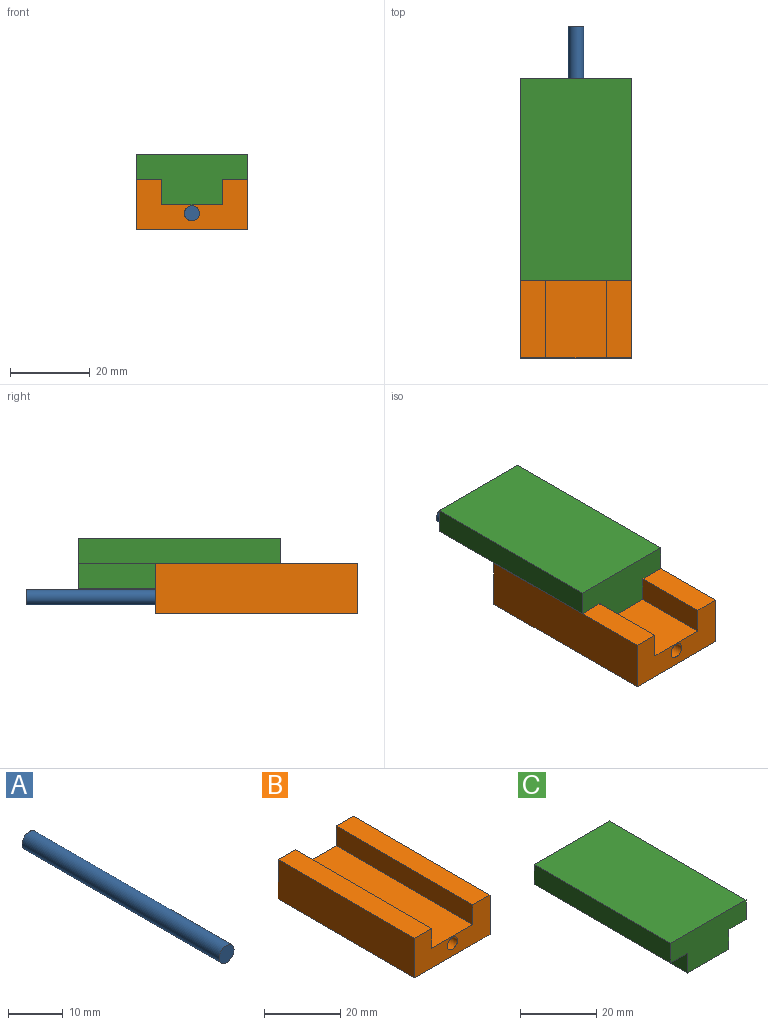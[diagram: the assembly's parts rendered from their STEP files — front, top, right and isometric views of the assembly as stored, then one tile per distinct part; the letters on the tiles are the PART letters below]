
ASSEMBLY  parts=3 mates=3
PART A: 3 faces, bbox 3.8x50.8x3.8 mm
  f0: cylinder r=1.91mm len=50.8mm, axis (0,1,0), area 608mm2, adj f1,f2
  f1: plane 3.81x3.81mm, normal (0,-1,0), area 11.4mm2, adj f0
  f2: plane 3.81x3.81mm, normal (0,1,0), area 11.4mm2, adj f0
PART B: 11 faces, bbox 27.9x50.8x12.7 mm
  f0: plane 50.8x12.7mm, normal (-1,0,0), area 645.2mm2, adj f1,f7,f8,f9
  f1: plane 50.8x27.94mm, normal (0,0,-1), area 1419.4mm2, adj f0,f2,f8,f9
  f2: plane 50.8x12.7mm, normal (1,0,0), area 645.2mm2, adj f1,f3,f8,f9
  f3: plane 50.8x6.35mm, normal (0,0,1), area 322.6mm2, adj f2,f4,f8,f9
  f4: plane 50.8x6.35mm, normal (-1,0,0), area 322.6mm2, adj f3,f5,f8,f9
  f5: plane 50.8x15.24mm, normal (0,0,1), area 774.2mm2, adj f4,f6,f8,f9
  f6: plane 50.8x6.35mm, normal (1,0,0), area 322.6mm2, adj f5,f7,f8,f9
  f7: plane 50.8x6.35mm, normal (0,0,1), area 322.6mm2, adj f0,f6,f8,f9
  f8: plane 27.94x12.7mm, normal (0,-1,0), area 246.7mm2, adj f0,f1,f2,f3,f4,f5,f6,f7
  f9: plane 27.94x12.7mm, normal (0,1,0), area 246.7mm2, adj f0,f1,f2,f3,f4,f5,f6,f7
  f10: cylinder r=1.91mm len=50.8mm, axis (0,1,0), area 608mm2, adj f8,f9
PART C: 10 faces, bbox 27.9x50.8x12.7 mm
  f0: plane 50.8x27.94mm, normal (0,0,1), area 1419.4mm2, adj f1,f7,f8,f9
  f1: plane 50.8x6.35mm, normal (-1,0,0), area 322.6mm2, adj f0,f2,f8,f9
  f2: plane 50.8x6.35mm, normal (0,0,-1), area 322.6mm2, adj f1,f3,f8,f9
  f3: plane 50.8x6.35mm, normal (-1,0,0), area 322.6mm2, adj f2,f4,f8,f9
  f4: plane 50.8x15.24mm, normal (0,0,-1), area 774.2mm2, adj f3,f5,f8,f9
  f5: plane 50.8x6.35mm, normal (1,0,0), area 322.6mm2, adj f4,f6,f8,f9
  f6: plane 50.8x6.35mm, normal (0,0,-1), area 322.6mm2, adj f5,f7,f8,f9
  f7: plane 50.8x6.35mm, normal (1,0,0), area 322.6mm2, adj f0,f6,f8,f9
  f8: plane 27.94x12.7mm, normal (0,-1,0), area 274.2mm2, adj f0,f1,f2,f3,f4,f5,f6,f7
  f9: plane 27.94x12.7mm, normal (0,1,0), area 274.2mm2, adj f0,f1,f2,f3,f4,f5,f6,f7
PLACE A rot(axis=(0,1,0),83.2deg) t=(-46.48,81.35,-27.18)mm
PLACE B t=(-24.06,48.79,-22.34)mm fixed
PLACE C t=(-24.06,68.27,3.18)mm
MATE planar B.f5 <-> C.f4  axis (0,0,1) through (-24.06,23.39,-22.34)mm
MATE planar C.f3 <-> B.f6  axis (-1,0,0) through (-31.68,42.87,-19.16)mm
MATE cylindrical A.f0 <-> B.f10  axis (0,1,0) through (-24.06,55.95,-24.52)mm
